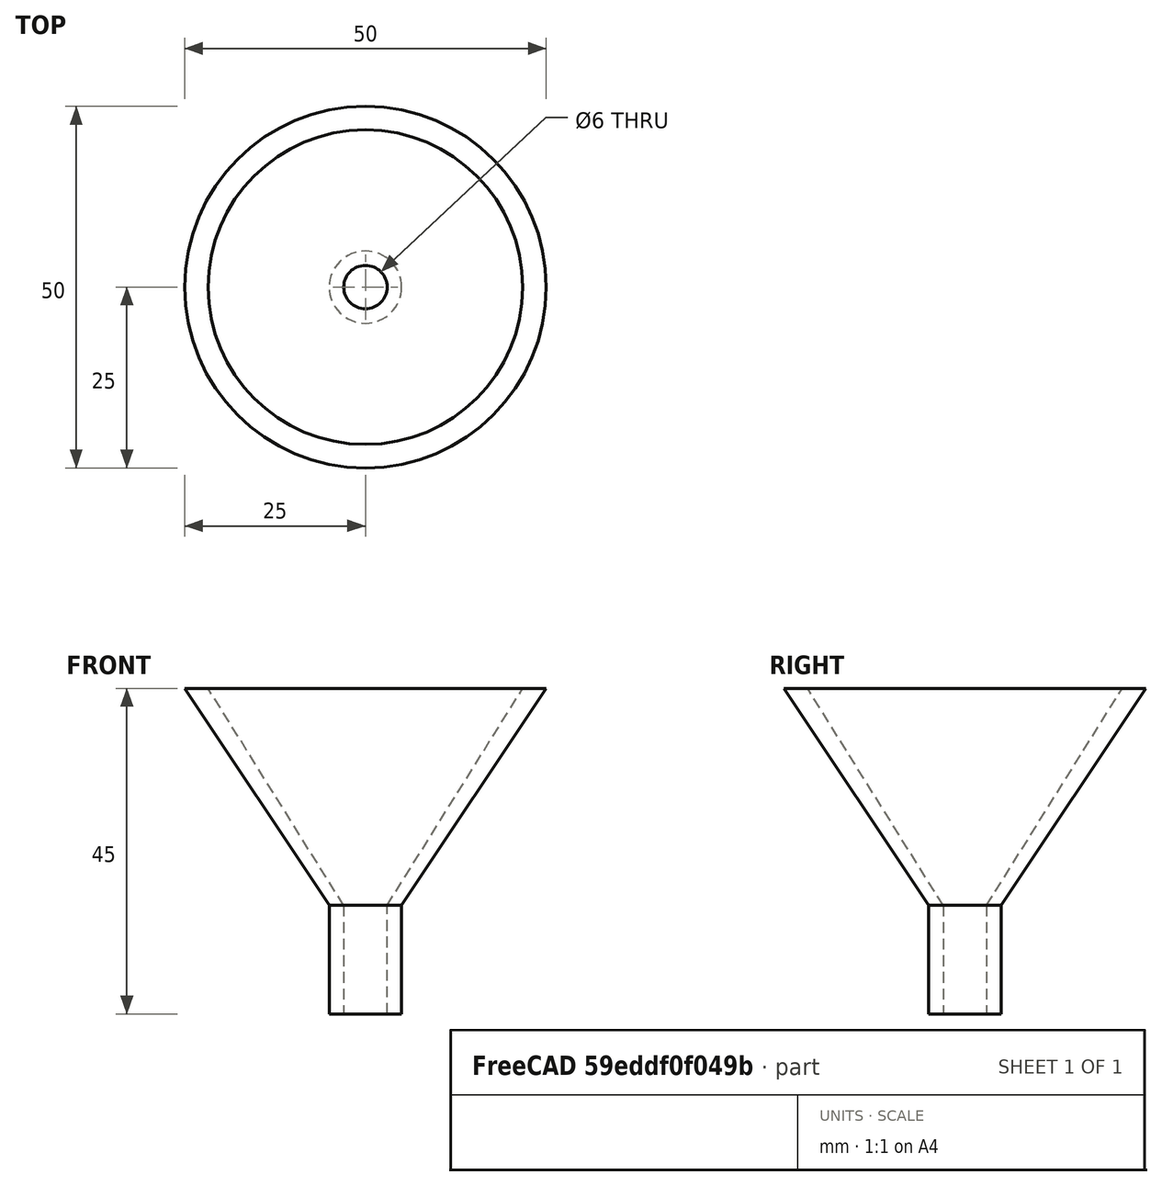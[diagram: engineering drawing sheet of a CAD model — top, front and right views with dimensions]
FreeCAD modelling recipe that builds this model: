
FCSTD DOCUMENT  (FreeCAD 0.21R33694 (Git))
Label: OJT1_T014R013_embut
License: All rights reserved
LicenseURL: http://en.wikipedia.org/wiki/All_rights_reserved
objects: Part::Cone×2, Part::Cylinder×2, Part::Cut×2
note: 6 computed .brp shape members not serialized (recipe doc carries the construction recipe); baked Part::Feature solids carry a one-line shape summary decoded from their .brp

FEATURE [Part::Cone] Cone
  Angle = 360
  AttacherType = Attacher::AttachEngine3D
  Height = 30
  Radius1 = 5
  Radius2 = 25
FEATURE [Part::Cylinder] Cylinder
  Angle = 360
  AttacherType = Attacher::AttachEngine3D
  FirstAngle = 0
  Height = 15
  Placement = pos=(0,0,-15) rot=(0,0,1;0rad)
  Radius = 5
  SecondAngle = 0
FEATURE [Part::Cone] Cone001
  Angle = 360
  AttacherType = Attacher::AttachEngine3D
  Height = 32
  Radius1 = 3
  Radius2 = 23
FEATURE [Part::Cut] Cut
  Base = -> Cone
  Refine = true
  Tool = -> Cone001
FEATURE [Part::Cylinder] Cylinder001
  Angle = 360
  AttacherType = Attacher::AttachEngine3D
  FirstAngle = 0
  Height = 23
  Placement = pos=(0,0,-19) rot=(0,0,1;0rad)
  Radius = 3
  SecondAngle = 0
FEATURE [Part::Cut] Cut001
  Base = -> Cylinder
  Refine = true
  Tool = -> Cylinder001
